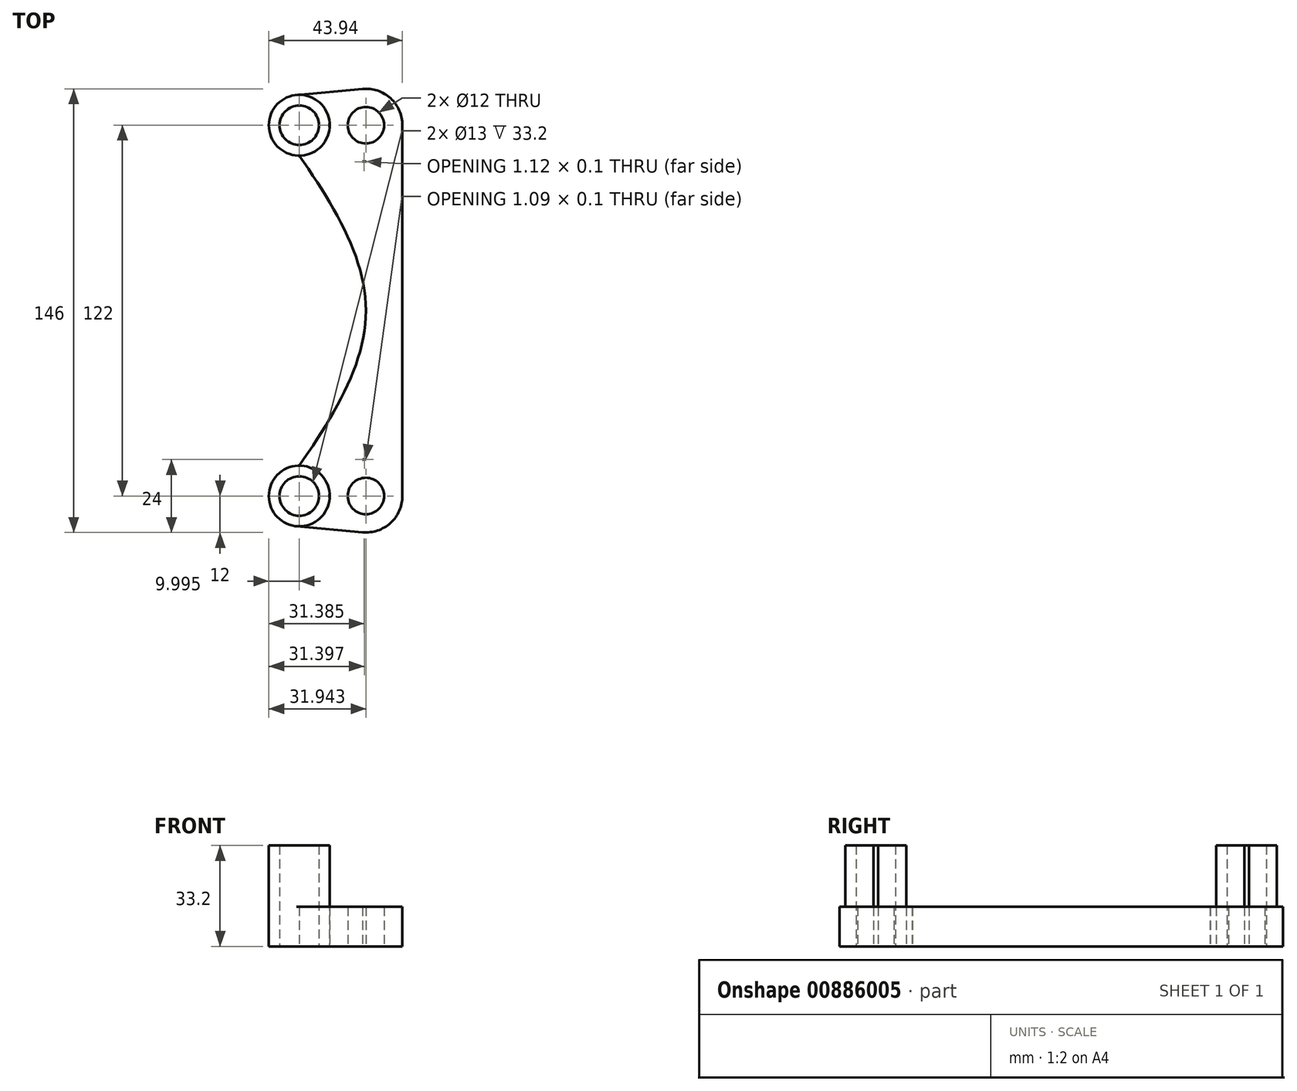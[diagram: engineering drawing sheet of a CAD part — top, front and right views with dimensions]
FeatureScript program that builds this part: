
annotation { "Feature Type Name" : "Feature", "Feature Type Description" : "" }
export const myFeature = defineFeature(function(context is Context, id is Id, definition is map)
    precondition{}
    {
        {
            var Q0;
            Q0=qCreatedBy(makeId("Top.planeOp"),FACE);
            var sketch = newSketch(context, id + "F0", { "sketchPlane" : qUnion([Q0])});
            skCircle(sketch, "E0", {"center": v(0, 0) * mm, "radius": 164 * mm, "construction": true});
            skCircle(sketch, "E1", {"center": v(0, 0) * mm, "radius": 83 * mm, "construction": true});
            skCircle(sketch, "E2", {"center": v(0, 0) * mm, "radius": 70 * mm, "construction": true});
            skCircle(sketch, "E3", {"center": v(-34.34, 61) * mm, "radius": 6 * mm});
            skCircle(sketch, "E4", {"center": v(-34.34, -61) * mm, "radius": 6 * mm});
            skLineSegment(sketch, "E5", {"start": v(-34.34, 61) * mm, "end": v(-34.34, -61) * mm});
            skCircle(sketch, "E6", {"center": v(-56.28, 61) * mm, "radius": 6.5 * mm});
            skCircle(sketch, "E7", {"center": v(-56.28, -61) * mm, "radius": 6.5 * mm});
            skLineSegment(sketch, "E8", {"start": v(-56.28, 61) * mm, "end": v(-56.28, -61) * mm, "construction": true});
            skLineSegment(sketch, "E9", {"start": v(-164, 0) * mm, "end": v(-117, 0) * mm, "construction": true});
            skLineSegment(sketch, "E10", {"start": v(-117, 0) * mm, "end": v(-83, 0) * mm, "construction": true});
            skCircle(sketch, "E11", {"center": v(-56.28, 61) * mm, "radius": 10 * mm});
            skCircle(sketch, "E12", {"center": v(-34.34, 61) * mm, "radius": 12 * mm});
            skCircle(sketch, "E13", {"center": v(-56.28, -61) * mm, "radius": 10 * mm});
            skCircle(sketch, "E14", {"center": v(-34.34, -61) * mm, "radius": 12 * mm});
            skLineSegment(sketch, "E15", {"start": v(-56.28, 61) * mm, "end": v(-66.28, 61) * mm, "construction": true});
            skLineSegment(sketch, "E16", {"start": v(-34.34, 61) * mm, "end": v(-22.34, 61) * mm, "construction": true});
            skLineSegment(sketch, "E17", {"start": v(-34.34, -61) * mm, "end": v(-22.34, -61) * mm, "construction": true});
            skLineSegment(sketch, "E18", {"start": v(-22.34, -61) * mm, "end": v(-22.34, 61) * mm});
            skLineSegment(sketch, "E19", {"start": v(-57.2, 70.96) * mm, "end": v(-35.43, 72.95) * mm});
            skLineSegment(sketch, "E20", {"start": v(-56.28, 51) * mm, "end": v(-34.34, 48.95) * mm});
            skLineSegment(sketch, "E21", {"start": v(-57.2, -70.96) * mm, "end": v(-35.43, -72.95) * mm});
            skFitSpline(sketch, "E22", {"points": [v(-56.28, 51) * mm, v(-34.34, 0) * mm, v(-56.28, -51) * mm], "startDerivative": vector(70.24, -101) * mm, "endDerivative": vector(-70.24, -101) * mm});
            skLineSegment(sketch, "E23", {"start": v(-57.2, -51.04) * mm, "end": v(-34.34, -48.95) * mm});
            skSolve(sketch);
        }
        {
            var Q0;
            {var subQ0=sQuery(id+"F0.wireOp",EDGE,"E20");var subQ1=sQuery(id+"F0.wireOp",EDGE,"E5");var subQ2=makeQuery(id+"F0.imprint","INTERSECT",VERTEX,{"derivedFrom":[subQ1,subQ0]});Q0=makeQuery(id+"F0.imprint","IMPRINT",FACE,{"disambiguationData":[TD([[makeQuery(id+"F0.imprint","IMPRINT",EDGE,{"disambiguationData":[TD([[subQ2,-1.0]])],"derivedFrom":subQ1}),-1.0]])]});}
            var Q1;
            {var subQ8=sQuery(id+"F0.wireOp",EDGE,"E18");Q1=makeQuery(id+"F0.imprint","IMPRINT",FACE,{"disambiguationData":[TD([[makeQuery(id+"F0.imprint","IMPRINT",EDGE,{"derivedFrom":subQ8}),1.0]])]});}
            var Q2;
            Q2=makeQuery(id+"F0.imprint","IMPRINT",FACE,{"disambiguationData":[TD([[makeQuery(id+"F0.imprint","IMPRINT",EDGE,{"derivedFrom":sQuery(id+"F0.wireOp",EDGE,"E3")}),-1.0]])]});
            var Q3;
            {var subQ1=sQuery(id+"F0.wireOp",EDGE,"E11");var subQ3=sQuery(id+"F0.wireOp",EDGE,"E12");var subQ4=makeQuery(id+"F0.imprint","INTERSECT",VERTEX,{"disambiguationData":[OD(1.0)],"derivedFrom":[subQ1,subQ3]});Q3=makeQuery(id+"F0.imprint","IMPRINT",FACE,{"disambiguationData":[TD([[makeQuery(id+"F0.imprint","IMPRINT",EDGE,{"disambiguationData":[TD([[subQ4,-1.0]])],"derivedFrom":subQ3}),-1.0]])]});}
            var Q4;
            {var subQ0=sQuery(id+"F0.wireOp",EDGE,"E19");Q4=makeQuery(id+"F0.imprint","IMPRINT",FACE,{"disambiguationData":[TD([[makeQuery(id+"F0.imprint","IMPRINT",EDGE,{"derivedFrom":subQ0}),-1.0]])]});}
            var Q5;
            Q5=makeQuery(id+"F0.imprint","IMPRINT",FACE,{"disambiguationData":[TD([[makeQuery(id+"F0.imprint","IMPRINT",EDGE,{"derivedFrom":sQuery(id+"F0.wireOp",EDGE,"E4")}),-1.0]])]});
            var Q6;
            {var subQ0=sQuery(id+"F0.wireOp",EDGE,"E23");var subQ1=sQuery(id+"F0.wireOp",EDGE,"E5");var subQ2=makeQuery(id+"F0.imprint","INTERSECT",VERTEX,{"derivedFrom":[subQ1,subQ0]});Q6=makeQuery(id+"F0.imprint","IMPRINT",FACE,{"disambiguationData":[TD([[makeQuery(id+"F0.imprint","IMPRINT",EDGE,{"disambiguationData":[TD([[subQ2,1.0]])],"derivedFrom":subQ1}),-1.0]])]});}
            var Q7;
            {var subQ0=sQuery(id+"F0.wireOp",EDGE,"E21");Q7=makeQuery(id+"F0.imprint","IMPRINT",FACE,{"disambiguationData":[TD([[makeQuery(id+"F0.imprint","IMPRINT",EDGE,{"derivedFrom":subQ0}),1.0]])]});}
            var Q8;
            {var subQ0=sQuery(id+"F0.wireOp",EDGE,"E22");var subQ1=sQuery(id+"F0.wireOp",EDGE,"E13");var subQ2=makeQuery(id+"F0.imprint","INTERSECT",VERTEX,{"derivedFrom":[subQ1,subQ0]});Q8=makeQuery(id+"F0.imprint","IMPRINT",FACE,{"disambiguationData":[TD([[makeQuery(id+"F0.imprint","IMPRINT",EDGE,{"disambiguationData":[TD([[subQ2,1.0]])],"derivedFrom":subQ1}),-1.0]])]});}
            extrude(context, id + "F1", {"entities" : qUnion([Q0, Q1, Q2, Q3, Q4, Q5, Q6, Q7, Q8]), "depth" : 13 * mm, "offsetDistance" : 25 * mm});
        }
        {
            var Q0;
            Q0=makeQuery(id+"F0.imprint","IMPRINT",FACE,{"disambiguationData":[TD([[makeQuery(id+"F0.imprint","IMPRINT",EDGE,{"derivedFrom":sQuery(id+"F0.wireOp",EDGE,"E6")}),-1.0]])]});
            var Q1;
            Q1=makeQuery(id+"F0.imprint","IMPRINT",FACE,{"disambiguationData":[TD([[makeQuery(id+"F0.imprint","IMPRINT",EDGE,{"derivedFrom":sQuery(id+"F0.wireOp",EDGE,"E7")}),-1.0]])]});
            extrude(context, id + "F2", {"entities" : qUnion([Q0, Q1]), "operationType" : NewBodyOperationType.ADD, "depth" : 33.2 * mm, "offsetDistance" : 25 * mm});
        }
    });
